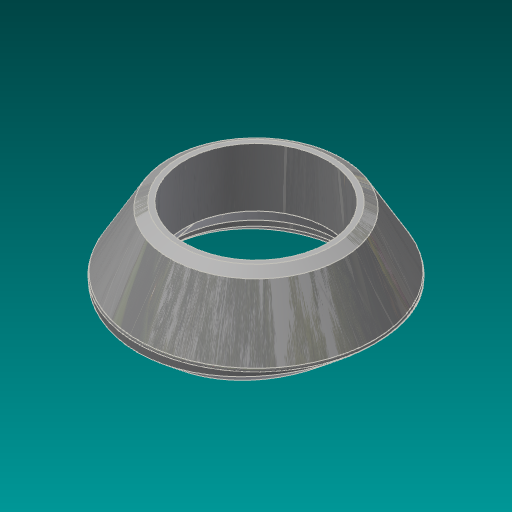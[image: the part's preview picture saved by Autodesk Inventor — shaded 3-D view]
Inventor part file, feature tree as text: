
AUTODESK INVENTOR PART (.ipt)
format: ipt  version: 2017.3 (Build 213257000, 257)  size: 430,080 bytes
history: native  units: mm (DEFAULTED — no unit token found)
features: other x7, sketch x5, plane x3, extrude x2, sweep x1, fillet x1
ambient origin geometry x8: Origin, YZ Plane, XZ Plane, XY Plane, X Axis, Y Axis, Z Axis, Center Point
bodies: Solid1 (feature_tree)
feature tree (19):
  sketch  "Sketch1"  dims[d5=44.45mm d8=90.0deg]
  plane  "Work Plane1"
  sketch  "Sketch2"  dims[d9=0.0mm d10=917.575mm]
  extrude  "Extrusion1"  TaperAngle=90.0deg  [1 undecoded]
  plane  "Work Plane2"
  sweep  "Sweep1"
  other  "Work Axis1"
  other  "Work Point1"
  other  "Work Point2"
  other  "Work Point3"
  plane  "Work Plane8"
  extrude  "Extrusion2"  [1 undecoded]
  fillet  "Fillet1"  Radius=73.66mm
  sketch  "Sketch3"  dims[d11=10.0mm d12=0.0mm d13=-503.2375mm d21=73.66mm]
  sketch  "3D Sketch1"
  other  "Edges3"
  other  "Edges4"
  other  "Work Axis2"
  sketch  "Sketch11"  dims[d22=6.0mm d23=4.0mm d24=2.0mm d25=90.0deg d26=30.1625mm d27=0.0mm d41=30.0deg d45=2.44475mm d50=39.37mm d51=44.45mm d52=122.2375mm d53=120.0deg d54=1191.41875mm d76=503.2375mm d77=0.0mm d79=2.19456mm d82=14.2875mm d83=8.290314mm d84=2.19456mm d85=0.0mm d86=0.0mm d87=90.0deg d88=0.0mm d89=90.0deg d90=93.6625mm d91=93.6625mm d92=0.0mm d93=-38.1mm d94=92.075mm d95=0.0mm d96=0.0mm d97=0.79375mm]
note: 2 required parameter values undecoded (feature->parameter linkage not recoverable at this tier; creation-order binding heuristic only, values carry confidence <= 0.55)
